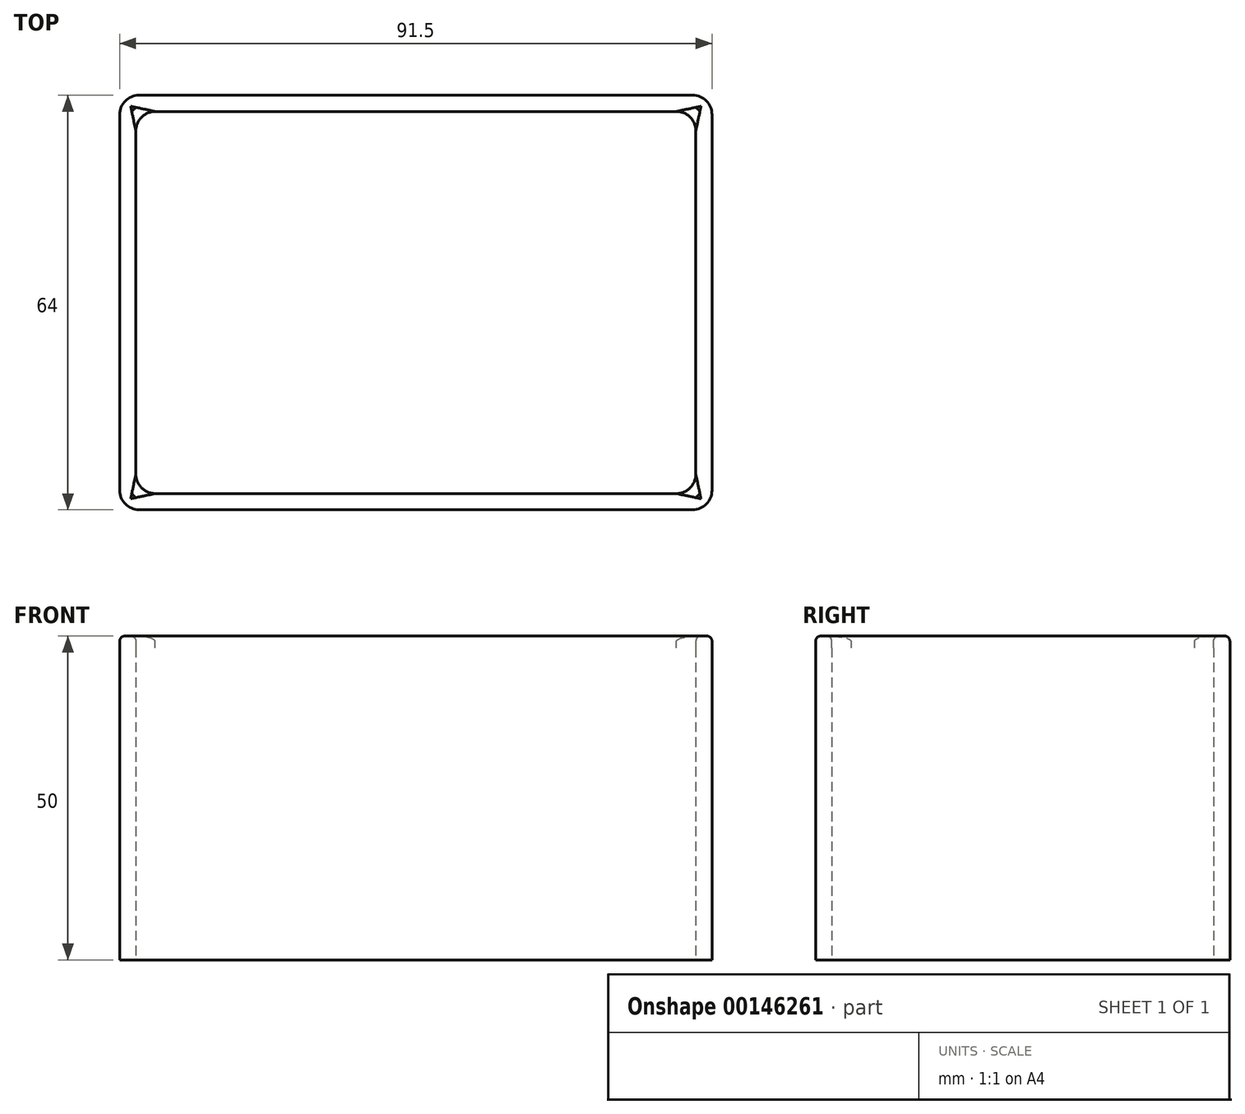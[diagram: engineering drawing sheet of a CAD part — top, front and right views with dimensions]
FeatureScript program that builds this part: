
annotation { "Feature Type Name" : "Feature", "Feature Type Description" : "" }
export const myFeature = defineFeature(function(context is Context, id is Id, definition is map)
    precondition{}
    {
        {
            var Q0;
            Q0=qCreatedBy(makeId("Top.planeOp"),FACE);
            var sketch = newSketch(context, id + "F0", { "sketchPlane" : qUnion([Q0])});
            skLineSegment(sketch, "E0.bottom", {"start": v(45.75, -32) * mm, "end": v(-45.75, -32) * mm});
            skLineSegment(sketch, "E0.top", {"start": v(45.75, 32) * mm, "end": v(-45.75, 32) * mm});
            skLineSegment(sketch, "E0.left", {"start": v(45.75, -32) * mm, "end": v(45.75, 32) * mm});
            skLineSegment(sketch, "E0.right", {"start": v(-45.75, -32) * mm, "end": v(-45.75, 32) * mm});
            skPoint(sketch, "E0.middle", {"position": v(0, 0) * mm});
            skLineSegment(sketch, "E1.bottom", {"start": v(43.25, -29.5) * mm, "end": v(-43.25, -29.5) * mm});
            skLineSegment(sketch, "E1.top", {"start": v(43.25, 29.5) * mm, "end": v(-43.25, 29.5) * mm});
            skLineSegment(sketch, "E1.left", {"start": v(43.25, -29.5) * mm, "end": v(43.25, 29.5) * mm});
            skLineSegment(sketch, "E1.right", {"start": v(-43.25, -29.5) * mm, "end": v(-43.25, 29.5) * mm});
            skSolve(sketch);
        }
        {
            var Q0;
            Q0=makeQuery(id+"F0.imprint","IMPRINT",FACE,{"disambiguationData":[TD([[makeQuery(id+"F0.imprint","IMPRINT",EDGE,{"derivedFrom":sQuery(id+"F0.wireOp",EDGE,"E0.bottom")}),-1.0]])]});
            extrude(context, id + "F1", {"entities" : qUnion([Q0]), "depth" : 50 * mm});
        }
        {
            var Q0;
            Q0=makeQuery(id+"F1.opExtrude","CAP_EDGE",EDGE,{"disambiguationData":[OSD([sQuery(id+"F0.wireOp",EDGE,"E0.bottom")])],"isStart":false});
            var Q1;
            Q1=makeQuery(id+"F1.opExtrude","CAP_EDGE",EDGE,{"disambiguationData":[OSD([sQuery(id+"F0.wireOp",EDGE,"E0.left")])],"isStart":false});
            var Q2;
            Q2=makeQuery(id+"F1.opExtrude","CAP_EDGE",EDGE,{"disambiguationData":[OSD([sQuery(id+"F0.wireOp",EDGE,"E0.top")])],"isStart":false});
            var Q3;
            Q3=makeQuery(id+"F1.opExtrude","CAP_EDGE",EDGE,{"disambiguationData":[OSD([sQuery(id+"F0.wireOp",EDGE,"E0.right")])],"isStart":false});
            var Q4;
            Q4=makeQuery(id+"F1.opExtrude","CAP_EDGE",EDGE,{"disambiguationData":[OSD([sQuery(id+"F0.wireOp",EDGE,"E1.right")])],"isStart":false});
            var Q5;
            Q5=makeQuery(id+"F1.opExtrude","CAP_EDGE",EDGE,{"disambiguationData":[OSD([sQuery(id+"F0.wireOp",EDGE,"E1.top")])],"isStart":false});
            var Q6;
            Q6=makeQuery(id+"F1.opExtrude","CAP_EDGE",EDGE,{"disambiguationData":[OSD([sQuery(id+"F0.wireOp",EDGE,"E1.left")])],"isStart":false});
            var Q7;
            Q7=makeQuery(id+"F1.opExtrude","CAP_EDGE",EDGE,{"disambiguationData":[OSD([sQuery(id+"F0.wireOp",EDGE,"E1.bottom")])],"isStart":false});
            fillet(context, id + "F2", {"entities" : qUnion([Q0, Q1, Q2, Q3, Q4, Q5, Q6, Q7]), "radius" : .8 * mm, "tangentPropagation" : true, "allowEdgeOverflow" : false});
        }
        {
            var Q0;
            Q0=makeQuery(id+"F1.opExtrude","SWEPT_EDGE",EDGE,{"disambiguationData":[OSD([sQuery(id+"F0.wireOp",EDGE,"E1.top"),sQuery(id+"F0.wireOp",EDGE,"E1.right")])]});
            var Q1;
            Q1=makeQuery(id+"F1.opExtrude","SWEPT_EDGE",EDGE,{"disambiguationData":[OSD([sQuery(id+"F0.wireOp",EDGE,"E1.bottom"),sQuery(id+"F0.wireOp",EDGE,"E1.right")])]});
            var Q2;
            Q2=makeQuery(id+"F1.opExtrude","SWEPT_EDGE",EDGE,{"disambiguationData":[OSD([sQuery(id+"F0.wireOp",EDGE,"E1.bottom"),sQuery(id+"F0.wireOp",EDGE,"E1.left")])]});
            var Q3;
            Q3=makeQuery(id+"F1.opExtrude","SWEPT_EDGE",EDGE,{"disambiguationData":[OSD([sQuery(id+"F0.wireOp",EDGE,"E1.top"),sQuery(id+"F0.wireOp",EDGE,"E1.left")])]});
            var Q4;
            Q4=makeQuery(id+"F1.opExtrude","SWEPT_EDGE",EDGE,{"disambiguationData":[OSD([sQuery(id+"F0.wireOp",EDGE,"E0.bottom"),sQuery(id+"F0.wireOp",EDGE,"E0.right")])]});
            var Q5;
            Q5=makeQuery(id+"F1.opExtrude","SWEPT_EDGE",EDGE,{"disambiguationData":[OSD([sQuery(id+"F0.wireOp",EDGE,"E0.bottom"),sQuery(id+"F0.wireOp",EDGE,"E0.left")])]});
            var Q6;
            Q6=makeQuery(id+"F1.opExtrude","SWEPT_EDGE",EDGE,{"disambiguationData":[OSD([sQuery(id+"F0.wireOp",EDGE,"E0.top"),sQuery(id+"F0.wireOp",EDGE,"E0.right")])]});
            var Q7;
            Q7=makeQuery(id+"F1.opExtrude","SWEPT_EDGE",EDGE,{"disambiguationData":[OSD([sQuery(id+"F0.wireOp",EDGE,"E0.top"),sQuery(id+"F0.wireOp",EDGE,"E0.left")])]});
            fillet(context, id + "F3", {"entities" : qUnion([Q0, Q1, Q2, Q3, Q4, Q5, Q6, Q7]), "radius" : 3 * mm, "tangentPropagation" : true, "allowEdgeOverflow" : false});
        }
    });
